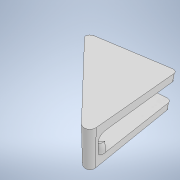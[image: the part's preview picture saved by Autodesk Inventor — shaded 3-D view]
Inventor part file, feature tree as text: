
AUTODESK INVENTOR PART (.ipt)
format: ipt  version: 2020.1 (Build 241239000, 239)  size: 169,984 bytes
history: native  units: mm
features: extrude x6, sketch x6, projected_geometry x4, fillet x3
ambient origin geometry x8: Origin, YZ Plane, XZ Plane, XY Plane, X Axis, Y Axis, Z Axis, Center Point
bodies: Solid1 (feature_tree)
feature tree (19):
  extrude  "Extrusion1"  Depth=40.0mm
  extrude  "Extrusion2"  Depth=14.0mm TaperAngle=0.0deg
  fillet  "Fillet1"  Radius=4.0mm
  extrude  "Extrusion3"  Depth=4.0mm TaperAngle=0.0deg
  extrude  "Extrusion4"  Depth=4.0mm TaperAngle=0.0deg
  extrude  "Extrusion5"  Depth=10.0mm TaperAngle=0.0deg
  extrude  "Extrusion6"  Depth=2.0mm
  fillet  "Fillet2"  Radius=2.0mm
  fillet  "Fillet3"  Radius=8.0mm
  sketch  "Sketch1"  dims[d0=40.0mm d1=40.0mm]
  sketch  "Sketch2"  dims[d2=56.568542mm d3=14.0mm d4=0.0mm d5=4.0mm]
  sketch  "Sketch4"  dims[d6=4.0mm d7=28.75mm d8=0.0mm]
  projected_geometry  "Projected Loop1"
  sketch  "Sketch5"  dims[d9=2.0mm d10=4.0mm d11=0.0mm]
  projected_geometry  "Projected Loop2"
  sketch  "Sketch6"  dims[d12=4.0mm d13=0.0mm d14=10.0mm d15=0.0mm]
  projected_geometry  "Projected Loop3"
  sketch  "Sketch7"  dims[d16=10.0mm d17=0.0mm d18=2.0mm d19=2.0mm d20=8.0mm]
  projected_geometry  "Projected Loop4"
